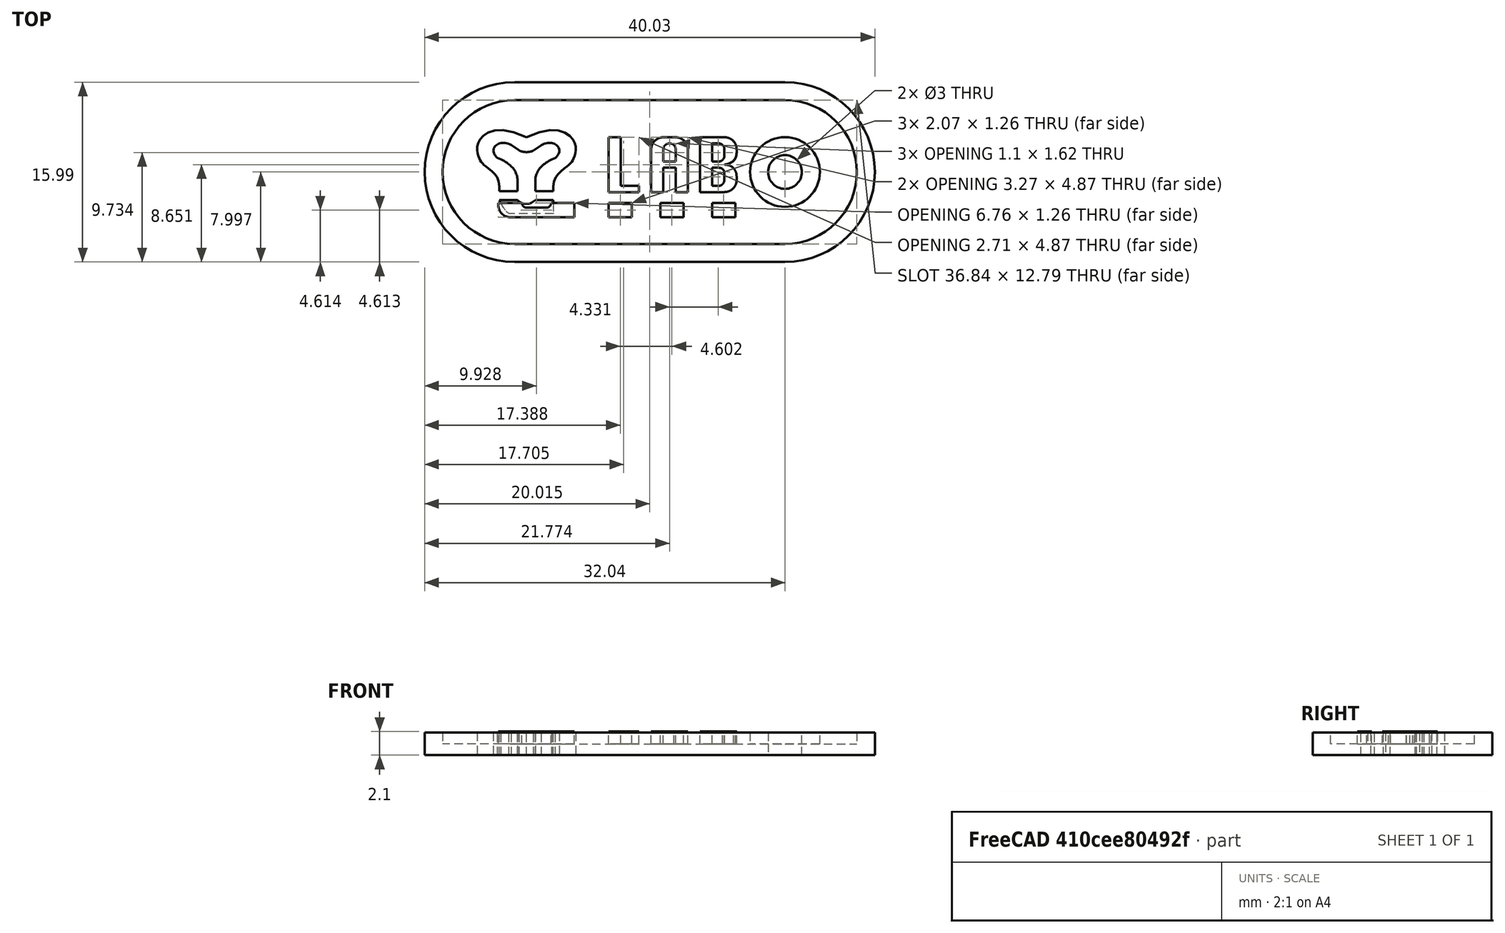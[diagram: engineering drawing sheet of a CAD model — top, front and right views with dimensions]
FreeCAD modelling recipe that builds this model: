
FCSTD DOCUMENT  (FreeCAD 0.20R29177 +426 (Git))
Label: YLabLogo
License: All rights reserved
LicenseURL: http://en.wikipedia.org/wiki/All_rights_reserved
objects: Sketcher::SketchObject×7, Part::Part2DObjectPython×6, Part::Extrusion×5, Part::Mirroring×2, PartDesign::Body×2, Part::FeaturePython×1, Part::MultiFuse×1, Mesh::Feature×1, Part::Fuse×1
note: 25 computed .brp shape members not serialized (recipe doc carries the construction recipe); baked Part::Feature solids carry a one-line shape summary decoded from their .brp

FEATURE [Part::Part2DObjectPython] ShapeString001  label="QM1"  # Draft 2D object (typed FeaturePython)
  FontFile = <path>
  Placement = pos=(-7,0,0) rot=(0,0,1;0rad)
  Size = 10
  String = ?
  Tracking = 0
FEATURE [Part::Part2DObjectPython] ShapeString002  label="QM2"  # Draft 2D object (typed FeaturePython)
  FontFile = <path>
  Placement = pos=(-12,0,0) rot=(0,0,1;0rad)
  Size = 10
  String = ?
  Tracking = 0
FEATURE [Part::Part2DObjectPython] ShapeString003  label="Dt1"  # Draft 2D object (typed FeaturePython)
  FontFile = <path>
  Placement = pos=(-0.4,0,0) rot=(0,0,1;0rad)
  Size = 10
  String = ...
  Tracking = 0
FEATURE [Part::Part2DObjectPython] ShapeString004  label="Dt2"  # Draft 2D object (typed FeaturePython)
  FontFile = <path>
  Placement = pos=(5,0,0) rot=(0,0,1;0rad)
  Size = 10
  String = .
  Tracking = 0
FEATURE [Part::Part2DObjectPython] ShapeString005  label="Dt3"  # Draft 2D object (typed FeaturePython)
  FontFile = <path>
  Placement = pos=(10,0,0) rot=(0,0,1;0rad)
  Size = 10
  String = .
  Tracking = 0
FEATURE [Part::Mirroring] mirror  label="QM2 (mirrored)"
  Base = (-8.28588,-0.0114783,0)
  Normal = (1,0,0)
  Placement = pos=(0.4,0,0) rot=(0,0,1;0rad)
  Source = -> ShapeString002
FEATURE [Part::Part2DObjectPython] ShapeString  label="LAB"  # Draft 2D object (typed FeaturePython)
  FontFile = <path>
  Placement = pos=(0,2.8,0) rot=(0,0,1;0rad)
  Size = 5.5
  String = LAB
  Tracking = 0
FEATURE [Sketcher::SketchObject] Sketch001  label="Lab"
  FullyConstrained = false
  sketch-geometry (53):
    g0: LineSegment StartX=0.517576 StartY=7.44006 StartZ=0 EndX=1.55071 EndY=7.44006 EndZ=0
    g1: LineSegment StartX=0.517576 StartY=2.8 StartZ=0 EndX=0.517576 EndY=7.44006 EndZ=0
    g2: LineSegment StartX=3.0974 StartY=2.8 StartZ=0 EndX=0.517576 EndY=2.8 EndZ=0
    g3: LineSegment StartX=3.0974 StartY=3.31556 StartZ=0 EndX=3.0974 EndY=2.8 EndZ=0
    g4: LineSegment StartX=1.55071 StartY=3.31556 StartZ=0 EndX=3.0974 EndY=3.31556 EndZ=0
    g5: LineSegment StartX=1.55071 StartY=7.44006 StartZ=0 EndX=1.55071 EndY=3.31556 EndZ=0
    g6: LineSegment StartX=7.23801 StartY=2.8 StartZ=0 EndX=6.20487 EndY=2.8 EndZ=0
    g7: LineSegment StartX=7.23801 StartY=6.3888 StartZ=0 EndX=7.23801 EndY=2.8 EndZ=0
    g8: BSplineCurve PolesCount=3 KnotsCount=2 Degree=2 IsPeriodic=0
    g9: BSplineCurve PolesCount=3 KnotsCount=2 Degree=2 IsPeriodic=0
    g10: LineSegment StartX=5.17173 StartY=7.44006 StartZ=0 EndX=6.18674 EndY=7.44006 EndZ=0
    g11: BSplineCurve PolesCount=3 KnotsCount=2 Degree=2 IsPeriodic=0
    g12: BSplineCurve PolesCount=3 KnotsCount=2 Degree=2 IsPeriodic=0
    g13: LineSegment StartX=4.12651 StartY=2.8 StartZ=0 EndX=4.12651 EndY=6.37067 EndZ=0
    g14: LineSegment StartX=5.15965 StartY=2.8 StartZ=0 EndX=4.12651 EndY=2.8 EndZ=0
    g15: LineSegment StartX=5.15965 StartY=4.86225 StartZ=0 EndX=5.15965 EndY=2.8 EndZ=0
    g16: LineSegment StartX=6.20487 StartY=4.86225 StartZ=0 EndX=5.15965 EndY=4.86225 EndZ=0
    g17: LineSegment StartX=6.20487 StartY=2.8 StartZ=0 EndX=6.20487 EndY=4.86225 EndZ=0
    g18: LineSegment StartX=6.20487 StartY=5.37781 StartZ=0 EndX=6.20487 EndY=6.38275 EndZ=0
    g19: LineSegment StartX=5.15965 StartY=5.37781 StartZ=0 EndX=6.20487 EndY=5.37781 EndZ=0
    g20: LineSegment StartX=5.15965 StartY=6.37671 StartZ=0 EndX=5.15965 EndY=5.37781 EndZ=0
    g21: BSplineCurve PolesCount=3 KnotsCount=2 Degree=2 IsPeriodic=0
    g22: BSplineCurve PolesCount=3 KnotsCount=2 Degree=2 IsPeriodic=0
    g23: BSplineCurve PolesCount=3 KnotsCount=2 Degree=2 IsPeriodic=0
    g24: BSplineCurve PolesCount=3 KnotsCount=2 Degree=2 IsPeriodic=0
    g25: LineSegment StartX=8.25101 StartY=2.8 StartZ=0 EndX=8.25101 EndY=7.44006 EndZ=0
    g26: LineSegment StartX=10.3052 StartY=2.8 StartZ=0 EndX=8.25101 EndY=2.8 EndZ=0
    g27: BSplineCurve PolesCount=3 KnotsCount=2 Degree=2 IsPeriodic=0
    g28: BSplineCurve PolesCount=3 KnotsCount=2 Degree=2 IsPeriodic=0
    g29: LineSegment StartX=11.3625 StartY=4.1171 StartZ=0 EndX=11.3625 EndY=3.83717 EndZ=0
    g30: BSplineCurve PolesCount=3 KnotsCount=2 Degree=2 IsPeriodic=0
    g31: BSplineCurve PolesCount=3 KnotsCount=2 Degree=2 IsPeriodic=0
    g32: BSplineCurve PolesCount=3 KnotsCount=2 Degree=2 IsPeriodic=0
    g33: LineSegment StartX=11.3625 StartY=6.39886 StartZ=0 EndX=11.3625 EndY=6.15317 EndZ=0
    g34: BSplineCurve PolesCount=3 KnotsCount=2 Degree=2 IsPeriodic=0
    g35: BSplineCurve PolesCount=3 KnotsCount=2 Degree=2 IsPeriodic=0
    g36: LineSegment StartX=8.25101 StartY=7.44006 StartZ=0 EndX=10.3535 EndY=7.44006 EndZ=0
    g37: LineSegment StartX=9.28415 StartY=3.31556 StartZ=0 EndX=9.77957 EndY=3.31556 EndZ=0
    g38: LineSegment StartX=9.28415 StartY=4.86225 StartZ=0 EndX=9.28415 EndY=3.31556 EndZ=0
    g39: LineSegment StartX=9.79769 StartY=4.86225 StartZ=0 EndX=9.28415 EndY=4.86225 EndZ=0
    g40: BSplineCurve PolesCount=3 KnotsCount=2 Degree=2 IsPeriodic=0
    g41: BSplineCurve PolesCount=3 KnotsCount=2 Degree=2 IsPeriodic=0
    g42: LineSegment StartX=10.3294 StartY=3.8714 StartZ=0 EndX=10.3294 EndY=4.3628 EndZ=0
    g43: BSplineCurve PolesCount=3 KnotsCount=2 Degree=2 IsPeriodic=0
    g44: BSplineCurve PolesCount=3 KnotsCount=2 Degree=2 IsPeriodic=0
    g45: LineSegment StartX=9.28415 StartY=5.37781 StartZ=0 EndX=9.79165 EndY=5.37781 EndZ=0
    g46: LineSegment StartX=9.28415 StartY=6.9245 StartZ=0 EndX=9.28415 EndY=5.37781 EndZ=0
    g47: LineSegment StartX=9.80373 StartY=6.9245 StartZ=0 EndX=9.28415 EndY=6.9245 EndZ=0
    g48: BSplineCurve PolesCount=3 KnotsCount=2 Degree=2 IsPeriodic=0
    g49: BSplineCurve PolesCount=3 KnotsCount=2 Degree=2 IsPeriodic=0
    g50: LineSegment StartX=10.3294 StartY=5.90747 StartZ=0 EndX=10.3294 EndY=6.39484 EndZ=0
    g51: BSplineCurve PolesCount=3 KnotsCount=2 Degree=2 IsPeriodic=0
    g52: BSplineCurve PolesCount=3 KnotsCount=2 Degree=2 IsPeriodic=0
  constraints (85):
    c: Horizontal(g0)
    c: Coincident(g0,g1)
    c: Vertical(g1)
    c: Coincident(g1,g2)
    c: Horizontal(g2)
    c: Coincident(g2,g3)
    c: Vertical(g3)
    c: Coincident(g3,g4)
    c: Horizontal(g4)
    c: Coincident(g4,g5)
    c: Vertical(g5)
    c: Coincident(g5,g0)
    c: Horizontal(g6)
    c: Coincident(g6,g7)
    c: Vertical(g7)
    c: Coincident(g7,g8)
    c: Coincident(g8,g9)
    c: Coincident(g9,g10)
    c: Horizontal(g10)
    c: Coincident(g10,g11)
    c: Coincident(g11,g12)
    c: Coincident(g12,g13)
    c: Vertical(g13)
    c: Coincident(g13,g14)
    c: Horizontal(g14)
    c: Coincident(g14,g15)
    c: Vertical(g15)
    c: Coincident(g15,g16)
    c: Horizontal(g16)
    c: Coincident(g16,g17)
    c: Vertical(g17)
    c: Coincident(g17,g6)
    c: Vertical(g18)
    c: Coincident(g18,g19)
    c: Horizontal(g19)
    c: Coincident(g19,g20)
    c: Vertical(g20)
    c: Coincident(g20,g21)
    c: Coincident(g21,g22)
    c: Coincident(g22,g23)
    c: Coincident(g23,g24)
    c: Coincident(g24,g18)
    c: Vertical(g25)
    c: Coincident(g25,g26)
    c: Horizontal(g26)
    c: Coincident(g26,g27)
    c: Coincident(g27,g28)
    c: Coincident(g28,g29)
    c: Vertical(g29)
    c: Coincident(g29,g30)
    c: Coincident(g30,g31)
    c: Coincident(g31,g32)
    c: Coincident(g32,g33)
    c: Vertical(g33)
    c: Coincident(g33,g34)
    c: Coincident(g34,g35)
    c: Coincident(g35,g36)
    c: Horizontal(g36)
    c: Coincident(g36,g25)
    c: Horizontal(g37)
    c: Coincident(g37,g38)
    c: Vertical(g38)
    c: Coincident(g38,g39)
    c: Horizontal(g39)
    c: Coincident(g39,g40)
    c: Coincident(g40,g41)
    c: Coincident(g41,g42)
    c: Vertical(g42)
    c: Coincident(g42,g43)
    c: Coincident(g43,g44)
    c: Coincident(g44,g37)
    c: Horizontal(g45)
    c: Coincident(g45,g46)
    c: Vertical(g46)
    c: Coincident(g46,g47)
    c: Horizontal(g47)
    c: Coincident(g47,g48)
    c: Coincident(g48,g49)
    c: Coincident(g49,g50)
    c: Vertical(g50)
    c: Coincident(g50,g51)
    c: Coincident(g51,g52)
    c: Coincident(g52,g45)
    c: Block(g38)
    c: Block(g1)
FEATURE [Sketcher::SketchObject] Sketch007  label="Y"
  ExternalGeometry = -> [Sketch001]
  FullyConstrained = false
  MapMode = 5
  Support = -> [XY_Plane]
  sketch-geometry (60):
    g0: LineSegment StartX=-8.1114 StartY=2.80363 StartZ=0 EndX=-8.1114 EndY=3.19534 EndZ=0
    g1-g6: Circle x6 (B-spline internal-alignment scaffolding for g7; pole/knot coordinates omitted)
    g7: BSplineCurve PolesCount=7 KnotsCount=5 Degree=3 IsPeriodic=0
    g8: GeomPoint X=-8.1114 Y=3.19534 Z=0
    g9: LineSegment StartX=-5.7114 StartY=9.79633 StartZ=0 EndX=-5.7114 EndY=-0.616301 EndZ=0
    g10: Circle CenterX=-7.04294 CenterY=6.89515 CenterZ=0 NormalX=0 NormalY=0 NormalZ=1 AngleXU=0 Radius=1
    g11: Circle CenterX=-8.08592 CenterY=7.50601 CenterZ=0 NormalX=0 NormalY=0 NormalZ=1 AngleXU=0 Radius=1
    g12: Circle CenterX=-9.25491 CenterY=6.58056 CenterZ=0 NormalX=0 NormalY=0 NormalZ=1 AngleXU=0 Radius=1
    g13: BSplineCurve PolesCount=4 KnotsCount=2 Degree=3 IsPeriodic=0
    g14: GeomPoint X=-7.04294 Y=6.89515 Z=0
    g15: GeomPoint X=-8.27341 Y=5.74973 Z=0
    g16: LineSegment StartX=-8.1114 StartY=2.80363 StartZ=0 EndX=-6.5114 EndY=2.80363 EndZ=0
    g17: Circle CenterX=-8.27341 CenterY=5.74973 CenterZ=0 NormalX=0 NormalY=0 NormalZ=1 AngleXU=0 Radius=1
    g18: LineSegment StartX=-8.27341 StartY=5.74973 StartZ=0 EndX=-7.97667 EndY=5.62638 EndZ=0
    g19: LineSegment StartX=-6.5114 StartY=2.80363 StartZ=0 EndX=-6.5114 EndY=3.40307 EndZ=0
    g20: Circle CenterX=-7.97667 CenterY=5.62638 CenterZ=0 NormalX=0 NormalY=0 NormalZ=1 AngleXU=0 Radius=1
    g21: Circle CenterX=-6.3446 CenterY=4.83924 CenterZ=0 NormalX=0 NormalY=0 NormalZ=1 AngleXU=0 Radius=1
    g22: Circle CenterX=-6.5114 CenterY=3.40307 CenterZ=0 NormalX=0 NormalY=0 NormalZ=1 AngleXU=0 Radius=1
    g23: BSplineCurve PolesCount=3 KnotsCount=2 Degree=2 IsPeriodic=0
    g24: GeomPoint X=-7.97667 Y=5.62638 Z=0
    g25: GeomPoint X=-6.5114 Y=3.40307 Z=0
    g26: LineSegment StartX=-7.04294 StartY=6.89515 StartZ=0 EndX=-6.3446 EndY=6.41008 EndZ=0
    g27: Circle CenterX=-6.3446 CenterY=6.41008 CenterZ=0 NormalX=0 NormalY=0 NormalZ=1 AngleXU=0 Radius=1
    g28: Circle CenterX=-6.13227 CenterY=6.28909 CenterZ=0 NormalX=0 NormalY=0 NormalZ=1 AngleXU=0 Radius=1
    g29: Circle CenterX=-5.7114 CenterY=6.26395 CenterZ=0 NormalX=0 NormalY=0 NormalZ=1 AngleXU=0 Radius=1
    g30: BSplineCurve PolesCount=3 KnotsCount=2 Degree=2 IsPeriodic=0
    g31: GeomPoint X=-6.3446 Y=6.41008 Z=0
    g32: GeomPoint X=-5.7114 Y=6.26395 Z=0
    g33: LineSegment StartX=-3.3114 StartY=2.80363 StartZ=0 EndX=-3.3114 EndY=3.19534 EndZ=0
    g34: Circle CenterX=-1.48597 CenterY=5.59422 CenterZ=0 NormalX=0 NormalY=0 NormalZ=1 AngleXU=0 Radius=1
    g35: Circle CenterX=-1.90144 CenterY=5.08575 CenterZ=0 NormalX=0 NormalY=0 NormalZ=1 AngleXU=0 Radius=1
    g36: Circle CenterX=-3.3114 CenterY=4.13297 CenterZ=0 NormalX=0 NormalY=0 NormalZ=1 AngleXU=0 Radius=1
    g37: BSplineCurve PolesCount=7 KnotsCount=5 Degree=3 IsPeriodic=0
    g38: GeomPoint X=-3.3114 Y=3.19534 Z=0
    g39: Circle CenterX=-4.37986 CenterY=6.89515 CenterZ=0 NormalX=0 NormalY=0 NormalZ=1 AngleXU=0 Radius=1
    g40: Circle CenterX=-3.33687 CenterY=7.50601 CenterZ=0 NormalX=0 NormalY=0 NormalZ=1 AngleXU=0 Radius=1
    g41: Circle CenterX=-2.16788 CenterY=6.58056 CenterZ=0 NormalX=0 NormalY=0 NormalZ=1 AngleXU=0 Radius=1
    g42: BSplineCurve PolesCount=4 KnotsCount=2 Degree=3 IsPeriodic=0
    g43: GeomPoint X=-4.37986 Y=6.89515 Z=0
    g44: GeomPoint X=-3.14939 Y=5.74973 Z=0
    g45: LineSegment StartX=-3.3114 StartY=2.80363 StartZ=0 EndX=-4.9114 EndY=2.80363 EndZ=0
    g46: Circle CenterX=-3.14939 CenterY=5.74973 CenterZ=0 NormalX=0 NormalY=0 NormalZ=1 AngleXU=0 Radius=1
    g47: LineSegment StartX=-3.14939 StartY=5.74973 StartZ=0 EndX=-3.44612 EndY=5.62638 EndZ=0
    g48: LineSegment StartX=-4.9114 StartY=2.80363 StartZ=0 EndX=-4.9114 EndY=3.40307 EndZ=0
    g49: Circle CenterX=-3.44612 CenterY=5.62638 CenterZ=0 NormalX=0 NormalY=0 NormalZ=1 AngleXU=0 Radius=1
    g50: Circle CenterX=-5.07819 CenterY=4.83924 CenterZ=0 NormalX=0 NormalY=0 NormalZ=1 AngleXU=0 Radius=1
    g51: Circle CenterX=-4.9114 CenterY=3.40307 CenterZ=0 NormalX=0 NormalY=0 NormalZ=1 AngleXU=0 Radius=1
    g52: BSplineCurve PolesCount=3 KnotsCount=2 Degree=2 IsPeriodic=0
    g53: GeomPoint X=-3.44612 Y=5.62638 Z=0
    g54: GeomPoint X=-4.9114 Y=3.40307 Z=0
    g55: LineSegment StartX=-4.37986 StartY=6.89515 StartZ=0 EndX=-5.07819 EndY=6.41008 EndZ=0
    g56: Circle CenterX=-5.07819 CenterY=6.41008 CenterZ=0 NormalX=0 NormalY=0 NormalZ=1 AngleXU=0 Radius=1
    g57: BSplineCurve PolesCount=3 KnotsCount=2 Degree=2 IsPeriodic=0
    g58: GeomPoint X=-5.07819 Y=6.41008 Z=0
    g59: GeomPoint X=-5.7114 Y=6.26395 Z=0
  constraints (84):
    c: Vertical(g0)
    c: Weight(g1) = 1
    c: Equal(g1, g2-g6) x5
    c: Coincident(g7,g0)
    c: InternalAlignment(g1-g6 -> g7) x6
    c: Coincident(g0,g8)
    c: Vertical(g9)
    c: Vertical(g6,g0)
    c: Weight(g10) = 1
    c: Equal(g10,g11)
    c: Equal(g10,g12)
    c: InternalAlignment(g10,g13)
    c: InternalAlignment(g11,g13)
    c: InternalAlignment(g12,g13)
    c: InternalAlignment(g14,g13)
    c: InternalAlignment(g15,g13)
    c: PointOnObject(g7,g9)
    c: Coincident(g16,g0)
    c: Horizontal(g16)
    c: DistanceX(g16,g16) = 1.6
    c: DistanceX(g16,g9) = 0.8
    c: InternalAlignment(g17,g13)
    c: Equal(g17,g10)
    c: Coincident(g18,g13)
    c: Coincident(g19,g16)
    c: Parallel(g19,g0)
    c: Weight(g20) = 1
    c: Coincident(g23,g18)
    c: Equal(g20,g21)
    c: Equal(g20,g22)
    c: Coincident(g23,g19)
    c: InternalAlignment(g20,g23)
    c: InternalAlignment(g21,g23)
    c: InternalAlignment(g22,g23)
    c: InternalAlignment(g24,g23)
    c: InternalAlignment(g25,g23)
    c: Coincident(g26,g13)
    c: Weight(g27) = 1
    c: Coincident(g30,g26)
    c: Equal(g27,g28)
    c: Equal(g27,g29)
    c: PointOnObject(g30,g9)
    c: InternalAlignment(g27,g30)
    c: InternalAlignment(g28,g30)
    c: InternalAlignment(g29,g30)
    c: InternalAlignment(g31,g30)
    c: InternalAlignment(g32,g30)
    c: Vertical(g33)
    c: Coincident(g37,g33)
    c: InternalAlignment(g34,g37)
    c: InternalAlignment(g35,g37)
    c: InternalAlignment(g36,g37)
    c: Coincident(g33,g38)
    c: Weight(g39) = 1
    c: Equal(g39,g40)
    c: Equal(g39,g41)
    c: InternalAlignment(g39,g42)
    c: InternalAlignment(g40,g42)
    c: InternalAlignment(g41,g42)
    c: InternalAlignment(g43,g42)
    c: InternalAlignment(g44,g42)
    c: Coincident(g45,g33)
    c: Horizontal(g45)
    c: InternalAlignment(g46,g42)
    c: Equal(g46,g39)
    c: Coincident(g47,g42)
    c: Coincident(g48,g45)
    c: Parallel(g48,g33)
    c: Weight(g49) = 1
    c: Coincident(g52,g47)
    c: Equal(g49,g50)
    c: Equal(g49,g51)
    c: Coincident(g52,g48)
    c: InternalAlignment(g49,g52)
    c: InternalAlignment(g50,g52)
    c: InternalAlignment(g51,g52)
    c: InternalAlignment(g53,g52)
    c: InternalAlignment(g54,g52)
    c: Coincident(g55,g42)
    c: Weight(g56) = 1
    c: Coincident(g57,g55)
    c: InternalAlignment(g56,g57)
    c: InternalAlignment(g58,g57)
    c: InternalAlignment(g59,g57)
FEATURE [Sketcher::SketchObject] Sketch005  label="YFoot"
  ExternalGeometry = -> [Sketch007]
  FullyConstrained = false
  MapMode = 5
  Support = -> [XY_Plane]
  sketch-geometry (9):
    g0: GeomPoint X=-2.01497 Y=2.8047 Z=0
    g1: LineSegment StartX=-8.1114 StartY=2.00363 StartZ=0 EndX=-6.5114 EndY=2.00363 EndZ=0
    g2: LineSegment StartX=-3.3114 StartY=2.00363 StartZ=0 EndX=-3.3114 EndY=0.803628 EndZ=0
    g3: LineSegment StartX=-3.3114 StartY=0.803628 StartZ=0 EndX=-7.26059 EndY=0.803628 EndZ=0
    g4: GeomPoint X=-6.5114 Y=2.00363 Z=0
    g5: GeomPoint X=-4.9114 Y=2.00363 Z=0
    g6: ArcOfCircle CenterX=-5.7114 CenterY=2.80363 CenterZ=0 NormalX=0 NormalY=0 NormalZ=1 AngleXU=0 Radius=1.13137 StartAngle=3.92699 EndAngle=5.49779
    g7: LineSegment StartX=-4.9114 StartY=2.00363 StartZ=0 EndX=-3.3114 EndY=2.00363 EndZ=0
    g8: ArcOfCircle CenterX=-5.7114 CenterY=2.80363 CenterZ=0 NormalX=0 NormalY=0 NormalZ=1 AngleXU=0 Radius=2.52982 StartAngle=3.46334 EndAngle=4.05333
  constraints (21):
    c: Coincident(g7,g2)
    c: Coincident(g2,g3)
    c: Horizontal(g1)
    c: Horizontal(g3)
    c: Vertical(g2)
    c: DistanceY(g2,g2) = 1.2
    c: PointOnObject(g5,g1)
    c: Vertical(g-3,g5)
    c: Coincident(g6,g5)
    c: Horizontal(g6,g-3)
    c: Horizontal(g7)
    c: Coincident(g7,g5)
    c: Equal(g7,g1)
    c: DistanceX(g1,g1) = 1.6
    c: Coincident(g8,g6)
    c: Coincident(g8,g1)
    c: Coincident(g8,g3)
    c: DistanceY(g1,g-4) = 0.8
    c: Vertical(g6,g-4)
    c: Coincident(g1,g4)
    c: Coincident(g1,g6)
FEATURE [Sketcher::SketchObject] Sketch003  label="Dots"
  ExternalGeometry = -> [Sketch001,Sketch005]
  FullyConstrained = false
  MapMode = 5
  Support = -> [XY_Plane]
  sketch-geometry (14):
    g0: LineSegment StartX=0.517576 StartY=2.40562 StartZ=0 EndX=2.3695 EndY=2.40562 EndZ=0
    g1: LineSegment StartX=2.3695 StartY=1.20562 StartZ=0 EndX=0.517576 EndY=1.20562 EndZ=0
    g2: LineSegment StartX=2.3695 StartY=2.40562 StartZ=0 EndX=2.3695 EndY=1.20562 EndZ=0
    g3: LineSegment StartX=4.93081 StartY=2.40562 StartZ=0 EndX=6.78273 EndY=2.40562 EndZ=0
    g4: LineSegment StartX=4.93081 StartY=1.20562 StartZ=0 EndX=4.93081 EndY=2.40562 EndZ=0
    g5: LineSegment StartX=6.78273 StartY=1.20562 StartZ=0 EndX=4.93081 EndY=1.20562 EndZ=0
    g6: LineSegment StartX=6.78273 StartY=2.40562 StartZ=0 EndX=6.78273 EndY=1.20562 EndZ=0
    g7: LineSegment StartX=9.34404 StartY=2.40562 StartZ=0 EndX=11.196 EndY=2.40562 EndZ=0
    g8: LineSegment StartX=9.34404 StartY=1.20562 StartZ=0 EndX=9.34404 EndY=2.40562 EndZ=0
    g9: LineSegment StartX=11.196 StartY=1.20562 StartZ=0 EndX=9.34404 EndY=1.20562 EndZ=0
    g10: LineSegment StartX=11.196 StartY=2.40562 StartZ=0 EndX=11.196 EndY=1.20562 EndZ=0
    g11: LineSegment StartX=0.517576 StartY=2.40562 StartZ=0 EndX=0.517576 EndY=1.20562 EndZ=0
    g12: LineSegment StartX=2.3695 StartY=1.20562 StartZ=0 EndX=4.93081 EndY=1.20562 EndZ=0
    g13: LineSegment StartX=6.78273 StartY=1.20562 StartZ=0 EndX=9.34404 EndY=1.20562 EndZ=0
  constraints (36):
    c: Horizontal(g0)
    c: Horizontal(g1)
    c: Coincident(g1,g2)
    c: Vertical(g2)
    c: Horizontal(g3)
    c: Coincident(g3,g4)
    c: Vertical(g4)
    c: Coincident(g4,g5)
    c: Horizontal(g5)
    c: Coincident(g5,g6)
    c: Vertical(g6)
    c: Coincident(g6,g3)
    c: Horizontal(g7)
    c: Coincident(g7,g8)
    c: Vertical(g8)
    c: Coincident(g8,g9)
    c: Horizontal(g9)
    c: Coincident(g9,g10)
    c: Vertical(g10)
    c: Horizontal(g0,g3)
    c: Horizontal(g0,g7)
    c: Horizontal(g5,g8)
    c: Horizontal(g4,g1)
    c: Coincident(g1,g11)
    c: Coincident(g0,g2)
    c: Coincident(g0,g11)
    c: Coincident(g8,g13)
    c: Coincident(g5,g13)
    c: Coincident(g4,g12)
    c: Coincident(g1,g12)
    c: Equal(g12,g13)
    c: Coincident(g7,g10)
    c: Equal(g0,g3)
    c: Equal(g3,g7)
    c: Vertical(g11)
    c: Equal(g11,g-5)
FEATURE [Sketcher::SketchObject] Sketch  label="YLogoText"
  FullyConstrained = true
  MapMode = 5
  Support = -> [XY_Plane]
FEATURE [PartDesign::Body] Body  label="Logo"
  Group = -> [Sketch001,Sketch003,Sketch005,Sketch007,Sketch]
  Origin = -> Origin
FEATURE [Part::Extrusion] Extrude  label="LogoTextExtruded"
  Base = -> Sketch
  Dir = (0,0,1)
  DirMode = 2
  FaceMakerClass = Part::FaceMakerBullseye
  LengthFwd = 2
  LengthRev = 0
  Solid = true
  Symmetric = false
FEATURE [Sketcher::SketchObject] Sketch009  label="BatchBase"
  FullyConstrained = false
  MapMode = 5
  Support = -> [XY_Plane001]
  sketch-geometry (5):
    g0: ArcOfCircle CenterX=-6.76885 CenterY=4.49689 CenterZ=0 NormalX=0 NormalY=0 NormalZ=1 AngleXU=0 Radius=6.39388 StartAngle=1.5708 EndAngle=4.71239
    g1: ArcOfCircle CenterX=17.2797 CenterY=4.49689 CenterZ=0 NormalX=0 NormalY=0 NormalZ=1 AngleXU=0 Radius=6.39388 StartAngle=4.71239 EndAngle=7.85398
    g2: LineSegment StartX=-6.76885 StartY=-1.89699 StartZ=0 EndX=17.2797 EndY=-1.89699 EndZ=0
    g3: LineSegment StartX=17.2797 StartY=10.8908 StartZ=0 EndX=-6.76885 EndY=10.8908 EndZ=0
    g4: Circle CenterX=17.2797 CenterY=4.49689 CenterZ=0 NormalX=0 NormalY=0 NormalZ=1 AngleXU=0 Radius=1.5
  constraints (8):
    c: Tangent(g0,g2) = -1.5708
    c: Tangent(g2,g1) = -1.5708
    c: Tangent(g1,g3) = -1.5708
    c: Tangent(g3,g0) = -1.5708
    c: Equal(g0,g1)
    c: Horizontal(g2)
    c: Coincident(g4,g1)
    c: Diameter(g4) = 3  'dia_keyring'
FEATURE [Sketcher::SketchObject] Sketch010  label="BatchWall"
  ExternalGeometry = -> [Sketch009]
  FullyConstrained = true
  MapMode = 5
  Support = -> [XY_Plane001]
  expr: Constraints[11] = <<BatchBase>>.Constraints.dia_keyring + .Constraints.wall_width * 2
  expr: Constraints[19] = .Constraints.wall_width
  sketch-geometry (10):
    g0: ArcOfCircle CenterX=-6.76885 CenterY=4.49689 CenterZ=0 NormalX=0 NormalY=0 NormalZ=1 AngleXU=0 Radius=6.39388 StartAngle=1.5708 EndAngle=4.71239
    g1: ArcOfCircle CenterX=17.2797 CenterY=4.49689 CenterZ=0 NormalX=0 NormalY=0 NormalZ=1 AngleXU=0 Radius=6.39388 StartAngle=4.71239 EndAngle=7.85398
    g2: LineSegment StartX=-6.76885 StartY=-1.89699 StartZ=0 EndX=17.2797 EndY=-1.89699 EndZ=0
    g3: LineSegment StartX=17.2797 StartY=10.8908 StartZ=0 EndX=-6.76885 EndY=10.8908 EndZ=0
    g4: Circle CenterX=17.2797 CenterY=4.49689 CenterZ=0 NormalX=0 NormalY=0 NormalZ=1 AngleXU=0 Radius=1.5
    g5: Circle CenterX=17.2797 CenterY=4.49689 CenterZ=0 NormalX=0 NormalY=0 NormalZ=1 AngleXU=0 Radius=3.1
    g6: ArcOfCircle CenterX=-6.76885 CenterY=4.49689 CenterZ=0 NormalX=0 NormalY=0 NormalZ=1 AngleXU=0 Radius=7.99388 StartAngle=1.5708 EndAngle=4.71239
    g7: ArcOfCircle CenterX=17.2797 CenterY=4.49689 CenterZ=0 NormalX=0 NormalY=0 NormalZ=1 AngleXU=0 Radius=7.99388 StartAngle=4.71239 EndAngle=7.85398
    g8: LineSegment StartX=-6.76885 StartY=-3.49699 StartZ=0 EndX=17.2797 EndY=-3.49699 EndZ=0
    g9: LineSegment StartX=17.2797 StartY=12.4908 StartZ=0 EndX=-6.76885 EndY=12.4908 EndZ=0
  constraints (22):
    c: Tangent(g0,g2) = -1.5708
    c: Tangent(g2,g1) = -1.5708
    c: Tangent(g1,g3) = -1.5708
    c: Tangent(g3,g0) = -1.5708
    c: Equal(g0,g1)
    c: Horizontal(g2)
    c: Coincident(g0,g-5)
    c: Coincident(g1,g-7)
    c: Coincident(g4,g1)
    c: Coincident(g5,g1)
    c: Tangent(g-3,g4)
    c: Diameter(g5) = 6.2
    c: Tangent(g6,g8) = -1.5708
    c: Tangent(g8,g7) = -1.5708
    c: Tangent(g7,g9) = -1.5708
    c: Tangent(g9,g6) = -1.5708
    c: Equal(g6,g7)
    c: Horizontal(g8)
    c: DistanceY(g0,g6) = 1.6  'wall_width'
    c: DistanceY(g6,g0) = 1.6
    c: Vertical(g1,g7)
    c: Vertical(g6,g0)
FEATURE [PartDesign::Body] Body001  label="SuppBadgeSketches"
  Group = -> [Sketch009,Sketch010]
  Origin = -> Origin001
FEATURE [Part::Extrusion] Extrude001  label="ExtrudeWall"
  Base = -> Sketch010
  Dir = (0,0,1)
  DirMode = 2
  FaceMakerClass = Part::FaceMakerBullseye
  LengthFwd = 2
  LengthRev = 0
  Solid = true
  Symmetric = false
FEATURE [Part::Extrusion] Extrude002  label="ExtrudeBase"
  Base = -> Sketch009
  Dir = (0,0,1)
  DirMode = 2
  FaceMakerClass = Part::FaceMakerBullseye
  LengthFwd = 1
  LengthRev = 0
  Solid = true
  Symmetric = false
FEATURE [Part::FeaturePython] Clone  label="LogoTextExtruded001"  # Draft clone (typed FeaturePython)
  AttacherType = Attacher::AttachEngine3D
  Fuse = false
  Objects = -> [Extrude]
  Placement = pos=(1.04731,-0.225047,0) rot=(0,0,1;0rad)
  Scale = (1.05,1.05,1.05)
FEATURE [Part::MultiFuse] Fusion  label="SupportBadge"
  Shapes = -> [Extrude001,Extrude002,Clone]
FEATURE [Mesh::Feature] Mesh  label="SupportBadge Mesh"
FEATURE [Part::Mirroring] Part__Mirroring  label="Y (Mirror #2)"
  Base = (0,0,0)
  Normal = (0,0,1)
  Source = -> Sketch007
FEATURE [Part::Extrusion] Extrude003  label="YFootExt"
  Base = -> Sketch005
  Dir = (0,0,1)
  DirMode = 2
  FaceMakerClass = Part::FaceMakerBullseye
  LengthFwd = 2
  LengthRev = 0
  Solid = true
  Symmetric = false
FEATURE [Part::Extrusion] Extrude004  label="YExt"
  Base = -> Sketch007
  Dir = (0,0,1)
  DirMode = 2
  FaceMakerClass = Part::FaceMakerBullseye
  LengthFwd = 2
  LengthRev = 0
  Solid = true
  Symmetric = false
FEATURE [Part::Fuse] Fusion001  label="YLogoExt"
  Base = -> Extrude003
  Tool = -> Extrude004
note: 6 file-system paths scrubbed to <path> (originals preserved in the JSON sidecar)
